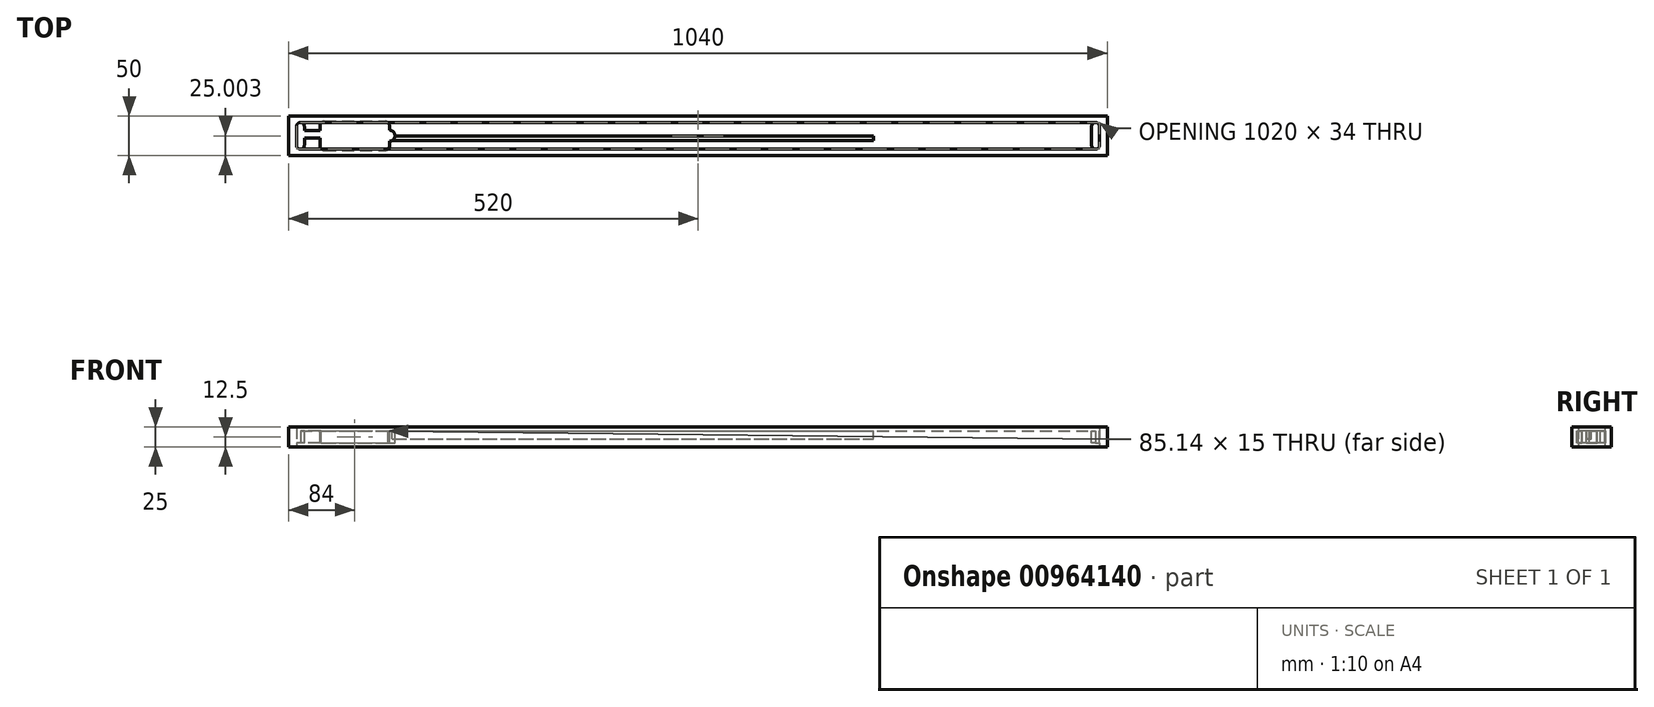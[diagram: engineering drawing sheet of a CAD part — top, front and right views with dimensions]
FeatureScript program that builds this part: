
annotation { "Feature Type Name" : "Feature", "Feature Type Description" : "" }
export const myFeature = defineFeature(function(context is Context, id is Id, definition is map)
    precondition{}
    {
        {
            var Q0;
            Q0=qCreatedBy(makeId("Top.planeOp"),FACE);
            var sketch = newSketch(context, id + "F0", { "sketchPlane" : qUnion([Q0])});
            skLineSegment(sketch, "E0.bottom", {"start": v(-499.85, 25.9) * mm, "end": v(540.15, 25.9) * mm});
            skLineSegment(sketch, "E0.top", {"start": v(-499.85, -24.1) * mm, "end": v(540.15, -24.1) * mm});
            skLineSegment(sketch, "E0.left", {"start": v(-499.85, 25.9) * mm, "end": v(-499.85, -24.1) * mm});
            skLineSegment(sketch, "E0.right", {"start": v(540.15, 25.9) * mm, "end": v(540.15, -24.1) * mm});
            skLineSegment(sketch, "E1.bottom", {"start": v(-484.85, 17.9) * mm, "end": v(525.15, 17.9) * mm});
            skLineSegment(sketch, "E1.top", {"start": v(-484.85, -16.1) * mm, "end": v(525.15, -16.1) * mm});
            skLineSegment(sketch, "E1.left", {"start": v(-489.85, 12.9) * mm, "end": v(-489.85, -11.1) * mm});
            skLineSegment(sketch, "E1.right", {"start": v(530.15, 12.9) * mm, "end": v(530.15, -11.1) * mm});
            skPoint(sketch, "E2.visualSharp", {"position": v(-489.85, 17.9) * mm});
            skArc(sketch, "E2.filletArc", {"start": v(-484.85, 17.9) * mm, "mid": v(-488.39, 16.43) * mm, "end": v(-489.85, 12.9) * mm});
            skPoint(sketch, "E3.visualSharp", {"position": v(-489.85, -16.1) * mm});
            skArc(sketch, "E3.filletArc", {"start": v(-489.85, -11.1) * mm, "mid": v(-488.39, -14.64) * mm, "end": v(-484.85, -16.1) * mm});
            skPoint(sketch, "E4.visualSharp", {"position": v(530.15, 17.9) * mm});
            skArc(sketch, "E4.filletArc", {"start": v(530.15, 12.9) * mm, "mid": v(528.69, 16.43) * mm, "end": v(525.15, 17.9) * mm});
            skPoint(sketch, "E5.visualSharp", {"position": v(530.15, -16.1) * mm});
            skArc(sketch, "E5.filletArc", {"start": v(525.15, -16.1) * mm, "mid": v(528.69, -14.64) * mm, "end": v(530.15, -11.1) * mm});
            skSolve(sketch);
        }
        {
            var Q0;
            Q0=makeQuery(id+"F0.imprint","IMPRINT",FACE,{"disambiguationData":[TD([[makeQuery(id+"F0.imprint","IMPRINT",EDGE,{"derivedFrom":sQuery(id+"F0.wireOp",EDGE,"E1.bottom")}),-1.0]])]});
            var sketch = newSketch(context, id + "F1", { "sketchPlane" : qUnion([Q0])});
            skPoint(sketch, "E6", {"position": v(-363.42, 3.72) * mm});
            skSolve(sketch);
        }
        {
            var Q0;
            Q0=makeQuery(id+"F0.imprint","IMPRINT",FACE,{"disambiguationData":[TD([[makeQuery(id+"F0.imprint","IMPRINT",EDGE,{"derivedFrom":sQuery(id+"F0.wireOp",EDGE,"E0.bottom")}),-1.0]])]});
            var Q1;
            Q1=makeQuery(id+"F1.imprint","IMPRINT",FACE,{"disambiguationData":[TD([[makeQuery(id+"F1.imprint","IMPRINT",EDGE,{"derivedFrom":makeQuery(id+"F0.imprint","IMPRINT",EDGE,{"derivedFrom":sQuery(id+"F0.wireOp",EDGE,"E1.bottom")})}),-1.0]])]});
            extrude(context, id + "F2", {"entities" : qUnion([Q0, Q1]), "depth" : 25 * mm, "offsetDistance" : 25 * mm});
        }
        {
            var Q0;
            Q0=makeQuery(id+"F2.opExtrude","CAP_FACE",FACE,{"disambiguationData":[OSD([sQuery(id+"F0.wireOp",EDGE,"E1.bottom"),sQuery(id+"F0.wireOp",EDGE,"E1.top"),sQuery(id+"F0.wireOp",EDGE,"E1.left"),sQuery(id+"F0.wireOp",EDGE,"E1.right"),sQuery(id+"F0.wireOp",EDGE,"E2.filletArc"),sQuery(id+"F0.wireOp",EDGE,"E3.filletArc"),sQuery(id+"F0.wireOp",EDGE,"E4.filletArc"),sQuery(id+"F0.wireOp",EDGE,"E5.filletArc")])],"isStart":false});
            extrude(context, id + "F3", {"entities" : qUnion([Q0]), "operationType" : NewBodyOperationType.REMOVE, "oppositeDirection" : true, "depth" : 5 * mm, "offsetDistance" : 25 * mm});
        }
        {
            var Q0;
            Q0=makeQuery(id+"F3.boolean.opBoolean","COPY",FACE,{"derivedFrom":makeQuery(id+"F3.opExtrude","CAP_FACE",FACE,{"disambiguationData":[OSD([sQuery(id+"F0.wireOp",EDGE,"E1.bottom"),sQuery(id+"F0.wireOp",EDGE,"E1.top"),sQuery(id+"F0.wireOp",EDGE,"E1.left"),sQuery(id+"F0.wireOp",EDGE,"E1.right"),sQuery(id+"F0.wireOp",EDGE,"E2.filletArc"),sQuery(id+"F0.wireOp",EDGE,"E3.filletArc"),sQuery(id+"F0.wireOp",EDGE,"E4.filletArc"),sQuery(id+"F0.wireOp",EDGE,"E5.filletArc")])],"isStart":false})});
            var sketch = newSketch(context, id + "F4", { "sketchPlane" : qUnion([Q0])});
            skLineSegment(sketch, "E7.bottom", {"start": v(-454.85, 19.4) * mm, "end": v(-376.85, 19.4) * mm});
            skLineSegment(sketch, "E7.top", {"start": v(-454.85, -17.6) * mm, "end": v(-376.85, -17.6) * mm});
            skLineSegment(sketch, "E7.left", {"start": v(-459.85, 14.4) * mm, "end": v(-459.85, -12.6) * mm});
            skLineSegment(sketch, "E7.right", {"start": v(-371.85, 14.4) * mm, "end": v(-371.85, -12.6) * mm});
            skPoint(sketch, "E8", {"position": v(-199.85, 0.9) * mm});
            skPoint(sketch, "E9", {"position": v(240.15, 0.9) * mm});
            skCircle(sketch, "E10", {"center": v(-371.8, 1.06) * mm, "radius": 7 * mm});
            skCircle(sketch, "E11", {"center": v(-484.85, 12.9) * mm, "radius": 5 * mm});
            skCircle(sketch, "E12", {"center": v(-484.85, -11.1) * mm, "radius": 5 * mm});
            skLineSegment(sketch, "E13.left", {"start": v(-489.85, 12.9) * mm, "end": v(-489.85, 12.9) * mm});
            skLineSegment(sketch, "E13.right", {"start": v(-479.85, 12.9) * mm, "end": v(-479.85, 12.9) * mm});
            skLineSegment(sketch, "E14.bottom", {"start": v(-489.85, 12.9) * mm, "end": v(-479.85, 12.9) * mm});
            skLineSegment(sketch, "E14.top", {"start": v(-489.85, -11.1) * mm, "end": v(-479.85, -11.1) * mm});
            skLineSegment(sketch, "E14.left", {"start": v(-489.85, 12.9) * mm, "end": v(-489.85, -11.1) * mm});
            skLineSegment(sketch, "E14.right", {"start": v(-479.85, 12.9) * mm, "end": v(-479.85, -11.1) * mm});
            skCircle(sketch, "E15", {"center": v(525.15, 12.9) * mm, "radius": 5 * mm});
            skCircle(sketch, "E16", {"center": v(525.15, -11.1) * mm, "radius": 5 * mm});
            skLineSegment(sketch, "E17.bottom", {"start": v(530.15, 12.9) * mm, "end": v(520.18, 12.9) * mm});
            skLineSegment(sketch, "E17.top", {"start": v(530.15, -11.66) * mm, "end": v(520.18, -11.66) * mm});
            skLineSegment(sketch, "E17.left", {"start": v(530.15, 12.9) * mm, "end": v(530.15, -11.66) * mm});
            skLineSegment(sketch, "E17.right", {"start": v(520.18, 12.9) * mm, "end": v(520.18, -11.66) * mm});
            skLineSegment(sketch, "E18.bottom", {"start": v(-459.85, 7.9) * mm, "end": v(-479.85, 7.9) * mm});
            skLineSegment(sketch, "E18.top", {"start": v(-459.85, -2.1) * mm, "end": v(-479.85, -2.1) * mm});
            skLineSegment(sketch, "E18.left", {"start": v(-459.85, 7.9) * mm, "end": v(-459.85, -2.1) * mm});
            skLineSegment(sketch, "E18.right", {"start": v(-479.85, 7.9) * mm, "end": v(-479.85, -2.1) * mm});
            skPoint(sketch, "E19.visualSharp", {"position": v(-459.85, 19.4) * mm});
            skArc(sketch, "E19.filletArc", {"start": v(-454.85, 19.4) * mm, "mid": v(-458.39, 17.93) * mm, "end": v(-459.85, 14.4) * mm});
            skPoint(sketch, "E20.visualSharp", {"position": v(-371.85, 19.4) * mm});
            skArc(sketch, "E20.filletArc", {"start": v(-371.85, 14.4) * mm, "mid": v(-373.31, 17.93) * mm, "end": v(-376.85, 19.4) * mm});
            skPoint(sketch, "E21.visualSharp", {"position": v(-371.85, -17.6) * mm});
            skArc(sketch, "E21.filletArc", {"start": v(-376.85, -17.6) * mm, "mid": v(-373.31, -16.14) * mm, "end": v(-371.85, -12.6) * mm});
            skPoint(sketch, "E22.visualSharp", {"position": v(-459.85, -17.6) * mm});
            skArc(sketch, "E22.filletArc", {"start": v(-459.85, -12.6) * mm, "mid": v(-458.39, -16.14) * mm, "end": v(-454.85, -17.6) * mm});
            skSolve(sketch);
        }
        {
            var Q0;
            Q0 = qSketchRegion(id + "F4", true);
            extrude(context, id + "F5", {"entities" : qUnion([Q0]), "operationType" : NewBodyOperationType.REMOVE, "oppositeDirection" : true, "depth" : 15 * mm, "offsetDistance" : 25 * mm});
        }
        {
            var Q0;
            {var subQ2=sQuery(id+"F4.wireOp",EDGE,"E10");var subQ4=sQuery(id+"F0.wireOp",EDGE,"E1.top");var subQ5=sQuery(id+"F0.wireOp",EDGE,"E1.bottom");Q0=makeQuery(id+"F5.boolean.opBoolean","SPLIT",FACE,{"disambiguationData":[TD([makeQuery(id+"F5.opExtrude","SWEPT_FACE",FACE,{"disambiguationData":[OSD([subQ2])]})])],"derivedFrom":makeQuery(id+"F3.boolean.opBoolean","COPY",FACE,{"derivedFrom":makeQuery(id+"F3.opExtrude","CAP_FACE",FACE,{"disambiguationData":[OSD([subQ5,subQ4,sQuery(id+"F0.wireOp",EDGE,"E1.left"),sQuery(id+"F0.wireOp",EDGE,"E1.right"),sQuery(id+"F0.wireOp",EDGE,"E2.filletArc"),sQuery(id+"F0.wireOp",EDGE,"E3.filletArc"),sQuery(id+"F0.wireOp",EDGE,"E4.filletArc"),sQuery(id+"F0.wireOp",EDGE,"E5.filletArc")])],"isStart":false})})});}
            var sketch = newSketch(context, id + "F6", { "sketchPlane" : qUnion([Q0])});
            skLineSegment(sketch, "E23.bottom", {"start": v(-376.85, 0.9) * mm, "end": v(243.15, 0.9) * mm});
            skLineSegment(sketch, "E23.top", {"start": v(-376.85, -5.1) * mm, "end": v(243.15, -5.1) * mm});
            skLineSegment(sketch, "E23.left", {"start": v(-376.85, 0.9) * mm, "end": v(-376.85, -5.1) * mm});
            skLineSegment(sketch, "E23.right", {"start": v(243.15, 0.9) * mm, "end": v(243.15, -5.1) * mm});
            skSolve(sketch);
        }
        {
            var Q0;
            Q0=makeQuery(id+"F6.imprint","IMPRINT",FACE,{"disambiguationData":[TD([[makeQuery(id+"F6.imprint","IMPRINT",EDGE,{"derivedFrom":sQuery(id+"F6.wireOp",EDGE,"E23.bottom")}),-1.0]])]});
            extrude(context, id + "F7", {"entities" : qUnion([Q0]), "operationType" : NewBodyOperationType.REMOVE, "oppositeDirection" : true, "depth" : 10 * mm, "offsetDistance" : 25 * mm});
        }
        {
            var Q0;
            Q0=sQuery(id+"F4.wireOp",VERTEX,"E9");
            var Q1;
            Q1=sQuery(id+"F4.wireOp",VERTEX,"E8");
            var Q2;
            Q2=makeQuery(id+"F2.opExtrude","SWEPT_BODY",BODY,{"disambiguationData":[OSD([sQuery(id+"F0.wireOp",EDGE,"E0.bottom"),sQuery(id+"F0.wireOp",EDGE,"E0.top"),sQuery(id+"F0.wireOp",EDGE,"E0.left"),sQuery(id+"F0.wireOp",EDGE,"E0.right"),sQuery(id+"F0.wireOp",EDGE,"E1.bottom"),sQuery(id+"F0.wireOp",EDGE,"E1.top"),sQuery(id+"F0.wireOp",EDGE,"E1.left"),sQuery(id+"F0.wireOp",EDGE,"E1.right"),sQuery(id+"F0.wireOp",EDGE,"E2.filletArc"),sQuery(id+"F0.wireOp",EDGE,"E3.filletArc"),sQuery(id+"F0.wireOp",EDGE,"E4.filletArc"),sQuery(id+"F0.wireOp",EDGE,"E5.filletArc")])]});
            hole(context, id + "F8", {"style" : HoleStyle.C_BORE, "endStyle" : HoleEndStyle.THROUGH, "holeDiameter" : 8 * mm, "cBoreDiameter" : 20 * mm, "cBoreDepth" : 15 * mm, "majorDiameter" : 5 * mm, "isTappedThrough" : true, "tappedDepth" : 12 * mm, "tapClearance" : 3, "startFromSketch" : true, "locations" : qUnion([Q0, Q1]), "scope" : qUnion([Q2])});
        }
    });
